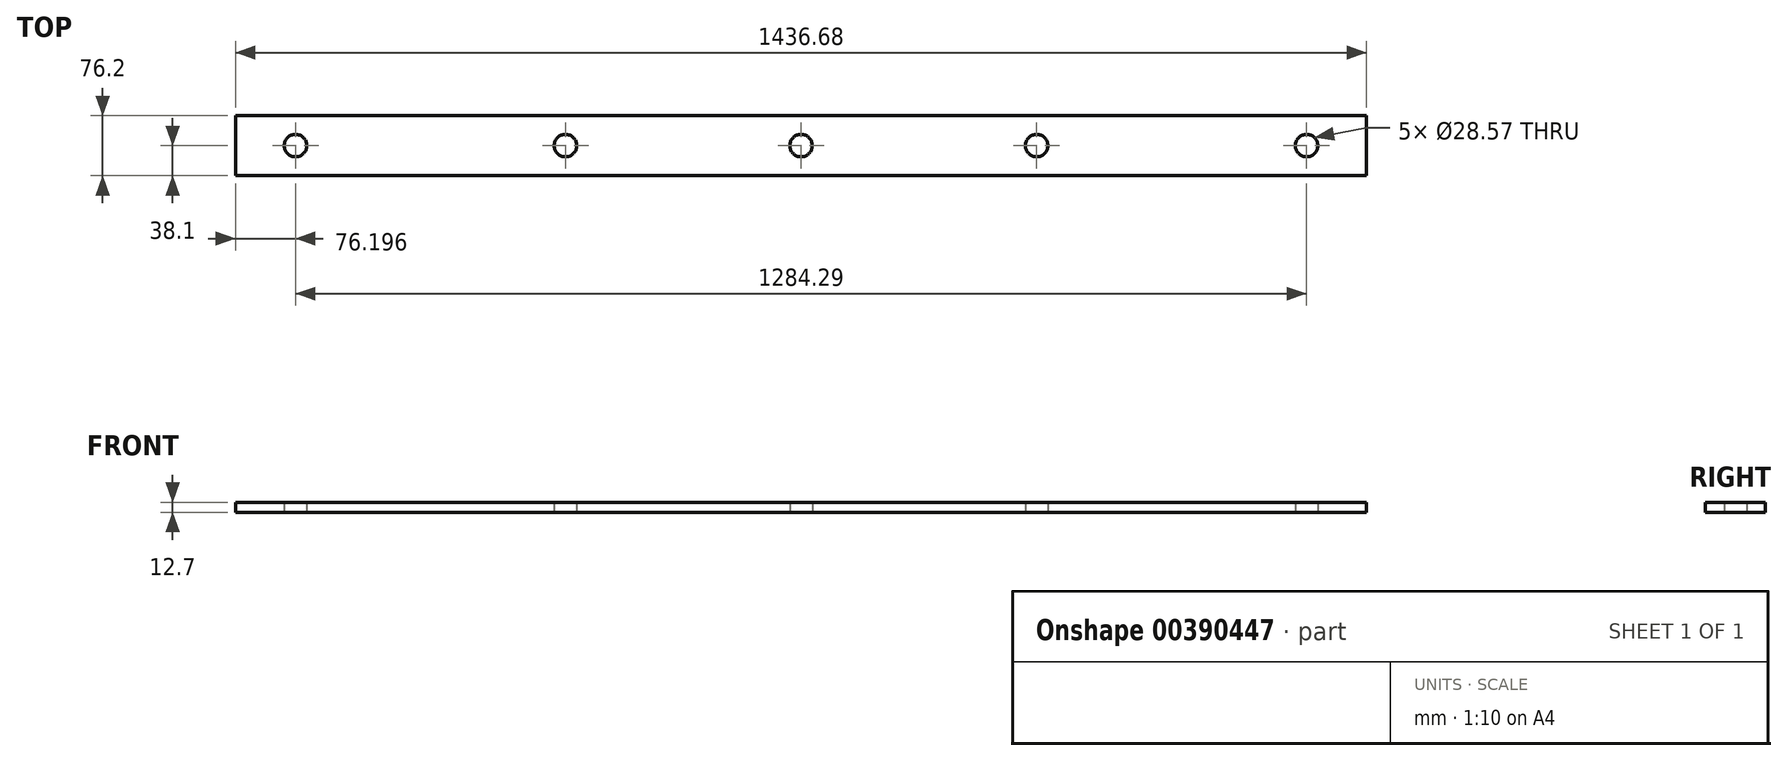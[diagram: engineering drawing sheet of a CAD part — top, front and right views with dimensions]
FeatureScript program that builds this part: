
annotation { "Feature Type Name" : "Feature", "Feature Type Description" : "" }
export const myFeature = defineFeature(function(context is Context, id is Id, definition is map)
    precondition{}
    {
        {
            var Q0;
            Q0=qCreatedBy(makeId("Top.planeOp"),FACE);
            var sketch = newSketch(context, id + "F0", { "sketchPlane" : qUnion([Q0])});
            skLineSegment(sketch, "E0.bottom", {"start": v(718.34, -38.1) * mm, "end": v(-718.34, -38.1) * mm});
            skLineSegment(sketch, "E0.top", {"start": v(718.34, 38.1) * mm, "end": v(-718.34, 38.1) * mm});
            skLineSegment(sketch, "E0.left", {"start": v(718.34, -38.1) * mm, "end": v(718.34, 38.1) * mm});
            skLineSegment(sketch, "E0.right", {"start": v(-718.34, -38.1) * mm, "end": v(-718.34, 38.1) * mm});
            skPoint(sketch, "E0.middle", {"position": v(0, 0) * mm});
            skCircle(sketch, "E1", {"center": v(-642.14, 0) * mm, "radius": 14.29 * mm});
            skPoint(sketch, "E1.centerSnap0", {"position": v(-718.34, 0) * mm});
            skCircle(sketch, "E2", {"center": v(-299.24, 0) * mm, "radius": 14.29 * mm});
            skCircle(sketch, "E3", {"center": v(0, 0) * mm, "radius": 14.29 * mm});
            skCircle(sketch, "E4.MirrorC", {"center": v(299.24, 0) * mm, "radius": 14.29 * mm});
            skCircle(sketch, "E5.MirrorC", {"center": v(642.14, 0) * mm, "radius": 14.29 * mm});
            skSolve(sketch);
        }
        {
            var Q0;
            Q0 = qSketchRegion(id + "F0", true);
            extrude(context, id + "F1", {"entities" : qUnion([Q0]), "depth" : 12.7 * mm});
        }
    });
